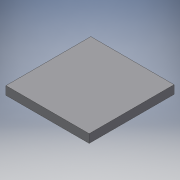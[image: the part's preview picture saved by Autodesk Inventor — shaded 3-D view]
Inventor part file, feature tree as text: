
AUTODESK INVENTOR PART (.ipt)
format: ipt  version: 2018 (Build 220112000, 112)  size: 93,696 bytes
history: native  units: mm
features: other x1, extrude x1, sketch x1
ambient origin geometry x8: Origin, YZ Plane, XZ Plane, XY Plane, X Axis, Y Axis, Z Axis, Center Point
bodies: Body1 (feature_tree)
feature tree (3):
  other  "Sólido1"
  extrude  "Extrusão1"  Depth=127.5mm
  sketch  "Esboço1"  dims[d0=125.0mm d1=127.5mm d2=12.7mm d3=0.0mm]
